# Revit family: ONRIZ
name_source: partatom
category: Mechanical Equipment
units: mm (PartAtom-declared; Revit-internal decimal feet)

## family parameters
Always vertical = Yes
Cut with Voids When Loaded = No
OmniClass Number = 23.40.40.11.17
OmniClass Title = Refrigerated Cases
Part Type = Normal
Room Calculation Point = No
Round Connector Dimension = Use Radius
Shared = No
Work Plane-Based = Yes

## types (5) — shared parameters
22" Shelf = Yes
Certifications = NSF 7, UL471, CSA
DATE = 02/08/2016
Default Elevation = 48"
Defrosts Per Day_2 = 1
Description = Narrow Back-to-Back Reach-In Glass Door Merchandiser
Discharge Air Velocity (FPM) = 400 (FPM)
EQUIPMENT DESCRIPTION = Narrow Back-to-Back Reach-In Glass Door Merchandiser
EQUIPMENT MARK = ONRIZ
Electric Defrost Fail-Safe = 46
Electric Defrost Run-Off Time (Min) = 0
Electric Defrost Termination Temp (°F) = 50
GLASS = Glass
Height = 81 1/4"
Hot Gas Defrost Fail-Safe = 24
Hot Gas Defrost Run-Off Time (Min) = 13 - 15
Hot Gas Defrost Termination = 73° F
Item Description = Narrow Back-to-Back Reach-In Glass Door Merchandiser
Legend Number = ONRIZ
Manufacturer = HILL PHOENIX
Model = ONRIZ
PAINTED METAL UPPER SHELF = PAINTED SHELVES
REFRIGERATION PIPING = COPPER PIPE
STAINLESS STEEL = GALVANIZED STEEL
Size of Door = 30"
Superheat Set Point @ Bulb (°F) = 3-5° F
Type of Door Swing = A-Swing
URL = http://www.hillphoenix.com
Width = 67 1/8"

## per-type parameters (varying)
- 2-Door Frozen (High): # of door=2; Application Discipline=Frozen; BTUH Conventional=891; BTUH Parallel=866; CENTER LINE & DRAIN=30"; DOOR CONFIGURATION=MASTER DOOR : 30" X 64 3/8" 2 DOOR A SWING (LEFT OPENING); Discharge Air (°F)=-1° F; Door Brand=ELMD/Polar RE (High); Evaporator (°F)=-7° F; Length=60"; Run-Off Time (Min)=13-1; SSD Combined Heated Rails Amps=2 A; SSD Combined Heated Rails Watts=206 W; SSD Combined Low E Rails Amps=2 A; SSD Combined Low E Rails Watts=181 W; SSD Crossfire/Polaris Amps=0 A; SSD Crossfire/Polaris Watts=30 W; SSD Defrost (Phase 1) 208 V Amps=8 A; SSD Defrost (Phase 1) 208 V Watts=1552 W; SSD Defrost (Phase 1) 240 V Amps=9 A; SSD Defrost (Phase 1) 240 V Watts=2068 W; SSD Defrost (Phase 3) 208 V Amps=7 A; SSD Defrost (Phase 3) 208 V Watts=1552 W; SSD Defrost (Phase 3) 240 V Amps=8 A; SSD Defrost (Phase 3) 240 V Watts=2068 W; SSD Fans Per Case=2; SSD GE Immersion Amps=0 A; SSD GE Immersion Watts=32 W; SSD High Efficiency Amps=1 A; SSD High Efficiency Watts=50 W; SSD Individual 101-LE Frame Amps=1 A; SSD Individual 101-LE Frame Watts=143 W; SSD Individual Heated Doors Amps=1 A; SSD Individual Heated Doors Watts=63 W; SSD Individual Low E Doors Amps=0 A; SSD Individual Low E Doors Watts=38 W; SSD Optimax Pro Amps=0 A; SSD Optimax Pro Watts=39 W; SSD Tank/Drain Heater Amps=1 A; SSD Tank/Drain Heater Watts=152 W
- 3-Door Frozen (High): # of door=3; Application Discipline=Frozen; BTUH Conventional=855; BTUH Parallel=831; CENTER LINE & DRAIN=45"; DOOR CONFIGURATION=MASTER DOOR : 30" X 64 3/8" 3 DOOR A SWING (LEFT OPENING); Discharge Air (°F)=-1° F; Door Brand=Eliminaator/2; Polar LE/EF (multi-door) Low Energy; Evaporator (°F)=-7° F; Length=90"; Run-Off Time (Min)=13-15 (Min); SSD Combined Heated Rails Amps=3 A; SSD Combined Heated Rails Watts=295 W; SSD Combined Low E Rails Amps=2 A; SSD Combined Low E Rails Watts=258 W; SSD Crossfire/Polaris Amps=0 A; SSD Crossfire/Polaris Watts=45 W; SSD Defrost (Phase 1) 208 V Amps=11 A; SSD Defrost (Phase 1) 208 V Watts=2274 W; SSD Defrost (Phase 1) 240 V Amps=13 A; SSD Defrost (Phase 1) 240 V Watts=3018 W; SSD Defrost (Phase 3) 208 V Amps=10 A; SSD Defrost (Phase 3) 208 V Watts=2274 W; SSD Defrost (Phase 3) 240 V Amps=11 A; SSD Defrost (Phase 3) 240 V Watts=3018 W; SSD Fans Per Case=3; SSD GE Immersion Amps=0 A; SSD GE Immersion Watts=48 W; SSD High Efficiency Amps=1 A; SSD High Efficiency Watts=75 W; SSD Individual 101-LE Frame Amps=2 A; SSD Individual 101-LE Frame Watts=200 W; SSD Individual Heated Doors Amps=1 A; SSD Individual Heated Doors Watts=95 W; SSD Individual Low E Doors Amps=0 A; SSD Individual Low E Doors Watts=58 W; SSD Optimax Pro Amps=1 A; SSD Optimax Pro Watts=58 W; SSD Tank/Drain Heater Amps=2 A; SSD Tank/Drain Heater Watts=171 W
- 4-Door Frozen (High): # of door=4; Application Discipline=Frozen; BTUH Conventional=891; BTUH Parallel=866; CENTER LINE & DRAIN=60"; DOOR CONFIGURATION=MASTER DOOR : 30" X 64 3/8" 4 DOOR A SWING (LEFT OPENING); Discharge Air (°F)=-1° F; Door Brand=ELMD/Polar RE (High); Evaporator (°F)=-7° F; Length=120"; Run-Off Time (Min)=13-15 (Min); SSD Combined Heated Rails Amps=4 A; SSD Combined Heated Rails Watts=388 W; SSD Combined Low E Rails Amps=3 A; SSD Combined Low E Rails Watts=338 W; SSD Crossfire/Polaris Amps=1 A; SSD Crossfire/Polaris Watts=60 W; SSD Defrost (Phase 1) 208 V Amps=14 A; SSD Defrost (Phase 1) 208 V Watts=2984 W; SSD Defrost (Phase 1) 240 V Amps=17 A; SSD Defrost (Phase 1) 240 V Watts=3992 W; SSD Defrost (Phase 3) 208 V Amps=12 A; SSD Defrost (Phase 3) 208 V Watts=2984 W; SSD Defrost (Phase 3) 240 V Amps=14 A; SSD Defrost (Phase 3) 240 V Watts=3992 W; SSD Fans Per Case=4; SSD GE Immersion Amps=1 A; SSD GE Immersion Watts=64 W; SSD High Efficiency Amps=1 A; SSD High Efficiency Watts=100 W; SSD Individual 101-LE Frame Amps=2 A; SSD Individual 101-LE Frame Watts=262 W; SSD Individual Heated Doors Amps=1 A; SSD Individual Heated Doors Watts=126 W; SSD Individual Low E Doors Amps=1 A; SSD Individual Low E Doors Watts=77 W; SSD Optimax Pro Amps=1 A; SSD Optimax Pro Watts=77 W; SSD Tank/Drain Heater Amps=2 A; SSD Tank/Drain Heater Watts=226 W
- 5-Door Frozen (High): # of door=5; Application Discipline=Ice Cream; BTUH Conventional=873; BTUH Parallel=848; CENTER LINE & DRAIN=75"; DOOR CONFIGURATION=MASTER DOOR : 30" X 64 3/8" 5 DOOR A SWING (LEFT OPENING); Discharge Air (°F)=-8° F; Door Brand=Eliminaator/2; Polar LE/EF (multi-door) Low Energy; Evaporator (°F)=-15° F; Length=150"; Run-Off Time (Min)=13-15 (Min); SSD Combined Heated Rails Amps=4 A; SSD Combined Heated Rails Watts=475 W; SSD Combined Low E Rails Amps=4 A; SSD Combined Low E Rails Watts=413 W; SSD Crossfire/Polaris Amps=1 A; SSD Crossfire/Polaris Watts=75 W; SSD Defrost (Phase 1) 208 V Amps=18 A; SSD Defrost (Phase 1) 208 V Watts=3640 W; SSD Defrost (Phase 1) 240 V Amps=20 A; SSD Defrost (Phase 1) 240 V Watts=4840 W; SSD Defrost (Phase 3) 208 V Amps=15 A; SSD Defrost (Phase 3) 208 V Watts=3640 W; SSD Defrost (Phase 3) 240 V Amps=17 A; SSD Defrost (Phase 3) 240 V Watts=4840 W; SSD Fans Per Case=5; SSD GE Immersion Amps=1 A; SSD GE Immersion Watts=80 W; SSD High Efficiency Amps=2 A; SSD High Efficiency Watts=125 W; SSD Individual 101-LE Frame Amps=3 A; SSD Individual 101-LE Frame Watts=317 W; SSD Individual Heated Doors Amps=2 A; SSD Individual Heated Doors Watts=158 W; SSD Individual Low E Doors Amps=1 A; SSD Individual Low E Doors Watts=96 W; SSD Optimax Pro Amps=1 A; SSD Optimax Pro Watts=96 W; SSD Tank/Drain Heater Amps=2 A; SSD Tank/Drain Heater Watts=275 W
- 6-Door Frozen (High): # of door=6; Application Discipline=Ice Cream; BTUH Conventional=928; BTUH Parallel=902; CENTER LINE & DRAIN=90"; DOOR CONFIGURATION=MASTER DOOR : 30" X 64 3/8" 6 DOOR A SWING (LEFT OPENING); Discharge Air (°F)=-8° F; Door Brand=ELMD/Polar RE; Evaporator (°F)=-15° F; Length=180"; Run-Off Time (Min)=13-15 (Min); SSD Combined Heated Rails Amps=5 A; SSD Combined Heated Rails Watts=565 W; SSD Combined Low E Rails Amps=4 A; SSD Combined Low E Rails Watts=491 W; SSD Crossfire/Polaris Amps=1 A; SSD Crossfire/Polaris Watts=90 W; SSD Defrost (Phase 1) 208 V Amps=20 A; SSD Defrost (Phase 1) 208 V Watts=4224 W; SSD Defrost (Phase 1) 240 V Amps=23 A; SSD Defrost (Phase 1) 240 V Watts=5624 W; SSD Defrost (Phase 3) 208 V Amps=18 A; SSD Defrost (Phase 3) 208 V Watts=4224 W; SSD Defrost (Phase 3) 240 V Amps=20 A; SSD Defrost (Phase 3) 240 V Watts=5624 W; SSD Fans Per Case=6; SSD GE Immersion Amps=1 A; SSD GE Immersion Watts=96 W; SSD High Efficiency Amps=2 A; SSD High Efficiency Watts=150 W; SSD Individual 101-LE Frame Amps=3 A; SSD Individual 101-LE Frame Watts=376 W; SSD Individual Heated Doors Amps=2 A; SSD Individual Heated Doors Watts=190 W; SSD Individual Low E Doors Amps=1 A; SSD Individual Low E Doors Watts=115 W; SSD Optimax Pro Amps=1 A; SSD Optimax Pro Watts=115 W; SSD Tank/Drain Heater Amps=3 A; SSD Tank/Drain Heater Watts=320 W

## geometry (parser evidence)
native form markers: Blend x8, Sweep x20
no freeform markers — native parametric forms only
